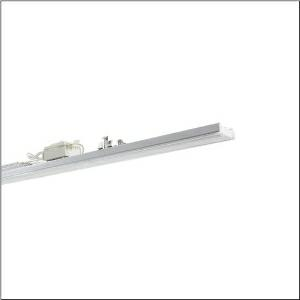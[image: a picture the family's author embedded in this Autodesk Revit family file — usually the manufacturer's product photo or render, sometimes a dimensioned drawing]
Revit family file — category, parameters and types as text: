
# Revit family: licross_r__21_recessed_ho_52tl12dn4axm_2663
name_source: partatom
category: Lighting Fixtures
units: mm (PartAtom-declared; Revit-internal decimal feet)

## family parameters
Cut with Voids When Loaded = No
Host = Face
Light Source = No
Part Type = Normal
Room Calculation Point = No
Round Connector Dimension = Use Diameter
Shared = No

## types (1)
- --- (1 x LED, 10000 lm, 54.6 W, 4000K)
    Apparent Load = 55 VA
    CIE Flux Codes = 69 91 98 100 100
    Color Rendering = 80
    Color Temperature = 4000K
    Default Elevation = 1800 mm
    Description = Licross® 21 Recessed HO, luminaire insert, of sheet steel, galvanised, coil coated, white, length: 1.500mm, width: 66mm, height: 67mm, LED rated luminous flux: 10.000lm, light colour: 840, control gear: DALI 2, with plug, 5-pole, with phase selection, mains connection: 220..240V, AC, 50/60Hz, rated input power: 55W, internal wiring halogen-free, primary optical cover: cover, of PMMA, light emission: direct distribution, primary light characteristic: symmetric, protection rating (complete): IP40, insulation class (complete): insulation class I (protective earthing), certification: CE, ENEC, VDE, UKCA, protection symbol: D if used in an environment without relevant dust loads with corresponding accessories, impact resistance: IK06, permissible ambient temperature for indoor applications: -25..+40°C, corresponds to IFS (International Featured Standards) requirements for safety and quality in the food industry, reducing of maximum allowable ambient temperature of 5°C with ceiling mounting, LABS conformity tested according to VDMA 24364:2018-05, packaging unit: 1 piece
    Height = 58 mm
    Lamp = 1 x LED
    Lamp Light Flux = 10000 lm
    Lamp Power = 54.6 W
    Lamp count = 1
    Length = 1500 mm
    Luminous efficacy = 183 lm/W
    Manufacturer = Siteco
    ModVariant = No
    Model = 52TL12DN4AXM
    Mounting Place = Ceiling
    Mounting Type = Pendant
    Number of Poles = 1
    OnlyDefault = Yes
    Power Factor = 1
    Product Name = Licross® 21 Recessed HO
    Product group = luminaire insert | ceiling pendant
    ProductGroupID = 902
    Protection Class = Protection class I
    Protection Degree = IP 40
    RLX_Detail_Level = 1
    RLX_Emergency_Light_Flux = 0 lm
    RLX_Emergency_Type = 0
    RLX_Emergency_Type_DB = No
    RlxData = <blob elided: 24445 chars, md5=f6715494>
    Socket = socket
    Standby Power = 0 W
    System Light Flux = 10000 lm
    System Power = 55 W
    Type Comments = factory setting: luminous flux: 100 % | dim-lin: 254 | 313 mA
    Type Image = l_1296930.jpg
    URL = http://relux.com
    VarID = @adj_138039
    Voltage = 0 V
    Weight = 0.00 kg
    Width = 66 mm

## geometry (parser evidence)
native form markers: Blend x4, Sweep x11
no freeform markers — native parametric forms only
